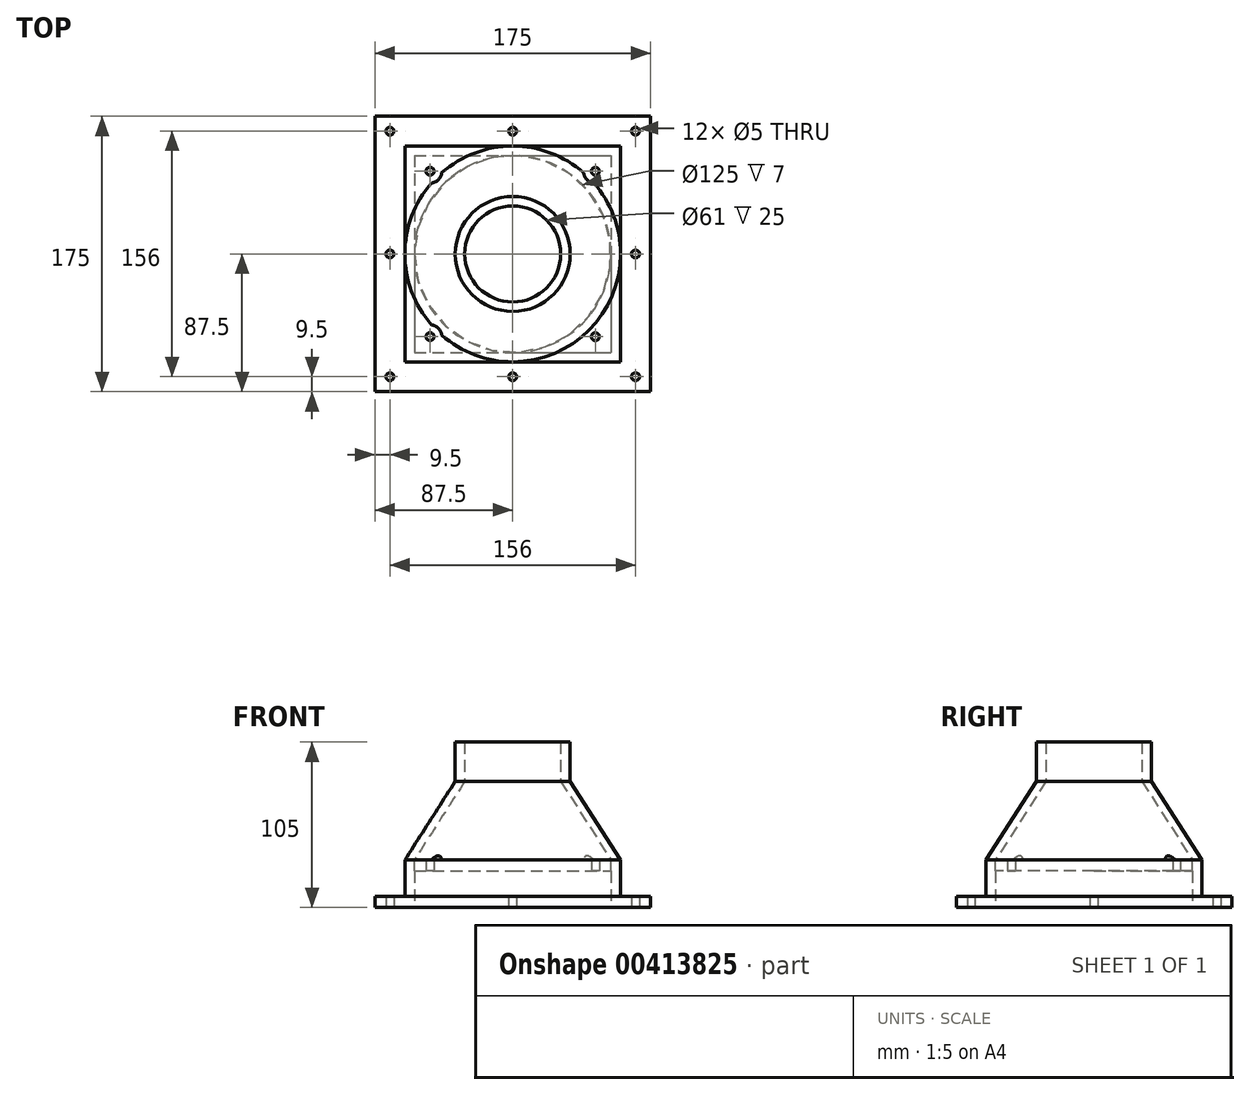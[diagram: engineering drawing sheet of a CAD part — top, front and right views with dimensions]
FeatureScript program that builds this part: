
annotation { "Feature Type Name" : "Feature", "Feature Type Description" : "" }
export const myFeature = defineFeature(function(context is Context, id is Id, definition is map)
    precondition{}
    {
        {
            var Q0;
            Q0=qCreatedBy(makeId("Top.planeOp"),FACE);
            var sketch = newSketch(context, id + "F0", { "sketchPlane" : qUnion([Q0])});
            skLineSegment(sketch, "E0.bottom", {"start": v(-62.5, 62.5) * mm, "end": v(62.5, 62.5) * mm});
            skLineSegment(sketch, "E0.top", {"start": v(-62.5, -62.5) * mm, "end": v(62.5, -62.5) * mm});
            skLineSegment(sketch, "E0.left", {"start": v(-62.5, 62.5) * mm, "end": v(-62.5, -62.5) * mm});
            skLineSegment(sketch, "E0.right", {"start": v(62.5, 62.5) * mm, "end": v(62.5, -62.5) * mm});
            skPoint(sketch, "E0.middle", {"position": v(0, 0) * mm});
            skLineSegment(sketch, "E1.bottom", {"start": v(-52.5, 52.5) * mm, "end": v(52.5, 52.5) * mm, "construction": true});
            skLineSegment(sketch, "E1.top", {"start": v(-52.5, -52.5) * mm, "end": v(52.5, -52.5) * mm, "construction": true});
            skLineSegment(sketch, "E1.left", {"start": v(-52.5, 52.5) * mm, "end": v(-52.5, -52.5) * mm, "construction": true});
            skLineSegment(sketch, "E1.right", {"start": v(52.5, 52.5) * mm, "end": v(52.5, -52.5) * mm, "construction": true});
            skLineSegment(sketch, "E2.bottom", {"start": v(-87.5, 87.5) * mm, "end": v(87.5, 87.5) * mm});
            skLineSegment(sketch, "E2.top", {"start": v(-87.5, -87.5) * mm, "end": v(87.5, -87.5) * mm});
            skLineSegment(sketch, "E2.left", {"start": v(-87.5, 87.5) * mm, "end": v(-87.5, -87.5) * mm});
            skLineSegment(sketch, "E2.right", {"start": v(87.5, 87.5) * mm, "end": v(87.5, -87.5) * mm});
            skLineSegment(sketch, "E3.0", {"start": v(-68.5, 68.5) * mm, "end": v(68.5, 68.5) * mm});
            skLineSegment(sketch, "E3.1", {"start": v(-68.5, 68.5) * mm, "end": v(-68.5, -68.5) * mm});
            skLineSegment(sketch, "E3.2", {"start": v(-68.5, -68.5) * mm, "end": v(68.5, -68.5) * mm});
            skLineSegment(sketch, "E3.3", {"start": v(68.5, 68.5) * mm, "end": v(68.5, -68.5) * mm});
            skCircle(sketch, "E4", {"center": v(0, 0) * mm, "radius": 62.5 * mm});
            skLineSegment(sketch, "E5.0", {"start": v(-78, 78) * mm, "end": v(78, 78) * mm, "construction": true});
            skLineSegment(sketch, "E5.1", {"start": v(-78, 78) * mm, "end": v(-78, -78) * mm, "construction": true});
            skLineSegment(sketch, "E5.2", {"start": v(-78, -78) * mm, "end": v(78, -78) * mm, "construction": true});
            skLineSegment(sketch, "E5.3", {"start": v(78, 78) * mm, "end": v(78, -78) * mm, "construction": true});
            skPoint(sketch, "E6", {"position": v(-78, 0) * mm});
            skPoint(sketch, "E7", {"position": v(0, -78) * mm});
            skPoint(sketch, "E8", {"position": v(78, 0) * mm});
            skPoint(sketch, "E9", {"position": v(0, 78) * mm});
            skSolve(sketch);
        }
        {
            var Q0;
            Q0=makeQuery(id+"F0.imprint","IMPRINT",FACE,{"disambiguationData":[TD([[makeQuery(id+"F0.imprint","IMPRINT",EDGE,{"derivedFrom":sQuery(id+"F0.wireOp",EDGE,"E2.bottom")}),-1.0]])]});
            extrude(context, id + "F1", {"entities" : qUnion([Q0]), "depth" : 7 * mm});
        }
        {
            var Q0;
            Q0=makeQuery(id+"F0.imprint","IMPRINT",FACE,{"disambiguationData":[TD([[makeQuery(id+"F0.imprint","IMPRINT",EDGE,{"derivedFrom":sQuery(id+"F0.wireOp",EDGE,"E0.bottom")}),1.0]])]});
            extrude(context, id + "F2", {"entities" : qUnion([Q0]), "operationType" : NewBodyOperationType.ADD, "depth" : 30 * mm});
        }
        {
            var Q0;
            Q0=makeQuery(id+"F2.opExtrude","CAP_FACE",FACE,{"disambiguationData":[OSD([sQuery(id+"F0.wireOp",EDGE,"E0.bottom"),sQuery(id+"F0.wireOp",EDGE,"E0.top"),sQuery(id+"F0.wireOp",EDGE,"E0.left"),sQuery(id+"F0.wireOp",EDGE,"E0.right"),sQuery(id+"F0.wireOp",EDGE,"E3.0"),sQuery(id+"F0.wireOp",EDGE,"E3.1"),sQuery(id+"F0.wireOp",EDGE,"E3.2"),sQuery(id+"F0.wireOp",EDGE,"E3.3")])],"isStart":false});
            var sketch = newSketch(context, id + "F3", { "sketchPlane" : qUnion([Q0])});
            skCircle(sketch, "E10.0", {"center": v(0, 0) * mm, "radius": 62.5 * mm});
            skLineSegment(sketch, "E11.0", {"start": v(-62.5, 62.5) * mm, "end": v(62.5, 62.5) * mm});
            skLineSegment(sketch, "E11.1", {"start": v(-62.5, 62.5) * mm, "end": v(-62.5, -62.5) * mm});
            skLineSegment(sketch, "E11.2", {"start": v(-62.5, -62.5) * mm, "end": v(62.5, -62.5) * mm});
            skLineSegment(sketch, "E11.3", {"start": v(62.5, 62.5) * mm, "end": v(62.5, -62.5) * mm});
            skCircle(sketch, "E12.0", {"center": v(0, 0) * mm, "radius": 68.5 * mm});
            skSolve(sketch);
        }
        {
            var Q0;
            {var subQ0=sQuery(id+"F3.wireOp",EDGE,"E11.1");var subQ1=sQuery(id+"F3.wireOp",EDGE,"E11.0");var subQ2=makeQuery(id+"F3.imprint","INTERSECT",VERTEX,{"derivedFrom":[subQ1,subQ0]});Q0=makeQuery(id+"F3.imprint","IMPRINT",FACE,{"disambiguationData":[TD([[makeQuery(id+"F3.imprint","IMPRINT",EDGE,{"disambiguationData":[TD([[subQ2,-1.0]])],"derivedFrom":subQ1}),-1.0]])]});}
            var Q1;
            Q1=makeQuery(id+"F3.imprint","IMPRINT",FACE,{"disambiguationData":[TD([[makeQuery(id+"F3.imprint","IMPRINT",EDGE,{"derivedFrom":sQuery(id+"F3.wireOp",EDGE,"E10.0")}),-1.0]])]});
            var Q2;
            {var subQ0=sQuery(id+"F3.wireOp",EDGE,"E11.3");var subQ1=sQuery(id+"F3.wireOp",EDGE,"E11.0");var subQ2=makeQuery(id+"F3.imprint","INTERSECT",VERTEX,{"derivedFrom":[subQ1,subQ0]});Q2=makeQuery(id+"F3.imprint","IMPRINT",FACE,{"disambiguationData":[TD([[makeQuery(id+"F3.imprint","IMPRINT",EDGE,{"disambiguationData":[TD([[subQ2,1.0]])],"derivedFrom":subQ1}),-1.0]])]});}
            var Q3;
            {var subQ0=sQuery(id+"F3.wireOp",EDGE,"E11.3");var subQ1=sQuery(id+"F3.wireOp",EDGE,"E11.2");var subQ2=makeQuery(id+"F3.imprint","INTERSECT",VERTEX,{"derivedFrom":[subQ1,subQ0]});Q3=makeQuery(id+"F3.imprint","IMPRINT",FACE,{"disambiguationData":[TD([[makeQuery(id+"F3.imprint","IMPRINT",EDGE,{"disambiguationData":[TD([[subQ2,1.0]])],"derivedFrom":subQ1}),1.0]])]});}
            var Q4;
            {var subQ0=sQuery(id+"F3.wireOp",EDGE,"E11.2");var subQ1=sQuery(id+"F3.wireOp",EDGE,"E11.1");var subQ2=makeQuery(id+"F3.imprint","INTERSECT",VERTEX,{"derivedFrom":[subQ1,subQ0]});Q4=makeQuery(id+"F3.imprint","IMPRINT",FACE,{"disambiguationData":[TD([[makeQuery(id+"F3.imprint","IMPRINT",EDGE,{"disambiguationData":[TD([[subQ2,1.0]])],"derivedFrom":subQ1}),1.0]])]});}
            extrude(context, id + "F4", {"entities" : qUnion([Q0, Q1, Q2, Q3, Q4]), "operationType" : NewBodyOperationType.ADD, "oppositeDirection" : true, "depth" : 7 * mm});
        }
        {
            var Q0;
            Q0=qCreatedBy(makeId("Front.planeOp"),FACE);
            var sketch = newSketch(context, id + "F5", { "sketchPlane" : qUnion([Q0])});
            skLineSegment(sketch, "E13", {"start": v(0, 0) * mm, "end": v(0, 80) * mm, "construction": true});
            skLineSegment(sketch, "E14", {"start": v(0, 80) * mm, "end": v(36.5, 80) * mm, "construction": true});
            skLineSegment(sketch, "E15", {"start": v(0, 80) * mm, "end": v(-30.5, 80) * mm, "construction": true});
            skLineSegment(sketch, "E16", {"start": v(-30.5, 80) * mm, "end": v(-36.5, 80) * mm, "construction": true});
            skLineSegment(sketch, "E17.0", {"start": v(-68.5, 30) * mm, "end": v(68.5, 30) * mm, "construction": true});
            skLineSegment(sketch, "E18", {"start": v(-68.5, 30) * mm, "end": v(-36.5, 80) * mm});
            skPoint(sketch, "E19", {"position": v(-62.5, 30) * mm});
            skLineSegment(sketch, "E20", {"start": v(-68.5, 30) * mm, "end": v(-62.5, 30) * mm});
            skLineSegment(sketch, "E21", {"start": v(-36.5, 80) * mm, "end": v(-30.5, 80) * mm});
            skLineSegment(sketch, "E22", {"start": v(-30.5, 80) * mm, "end": v(-62.5, 30) * mm});
            skSolve(sketch);
        }
        {
            var Q0;
            Q0=makeQuery(id+"F5.imprint","IMPRINT",FACE,{"disambiguationData":[TD([[makeQuery(id+"F5.imprint","IMPRINT",EDGE,{"derivedFrom":sQuery(id+"F5.wireOp",EDGE,"E18")}),-1.0]])]});
            var Q1;
            Q1=sQuery(id+"F5.wireOp",EDGE,"E13");
            revolve(context, id + "F6", {"operationType" : NewBodyOperationType.ADD, "entities" : qUnion([Q0]), "axis" : qUnion([Q1]), "revolveType" : RevolveType.FULL});
        }
        {
            var Q0;
            Q0=makeQuery(id+"F6.opRevolve","SWEPT_FACE",FACE,{"disambiguationData":[OSD([sQuery(id+"F5.wireOp",EDGE,"E21")])]});
            extrude(context, id + "F7", {"entities" : qUnion([Q0]), "operationType" : NewBodyOperationType.ADD, "depth" : 25 * mm});
        }
        {
            var Q0;
            Q0=sQuery(id+"F0.wireOp",VERTEX,"E1.left.start");
            var Q1;
            Q1=makeQuery(id+"F1.opExtrude","SWEPT_BODY",BODY,{"disambiguationData":[OSD([sQuery(id+"F0.wireOp",EDGE,"E2.bottom"),sQuery(id+"F0.wireOp",EDGE,"E2.top"),sQuery(id+"F0.wireOp",EDGE,"E2.left"),sQuery(id+"F0.wireOp",EDGE,"E2.right"),sQuery(id+"F0.wireOp",EDGE,"E3.0"),sQuery(id+"F0.wireOp",EDGE,"E3.1"),sQuery(id+"F0.wireOp",EDGE,"E3.2"),sQuery(id+"F0.wireOp",EDGE,"E3.3")])]});
            hole(context, id + "F8", {"style" : HoleStyle.SIMPLE, "endStyle" : HoleEndStyle.THROUGH, "oppositeDirection" : true, "holeDiameter" : 5 * mm, "isTappedThrough" : true, "tappedDepth" : 12 * mm, "tapClearance" : 3, "locations" : qUnion([Q0]), "scope" : qUnion([Q1])});
        }
        {
            var Q0;
            Q0=sQuery(id+"F0.wireOp",VERTEX,"E1.bottom.end");
            var Q1;
            Q1=makeQuery(id+"F1.opExtrude","SWEPT_BODY",BODY,{"disambiguationData":[OSD([sQuery(id+"F0.wireOp",EDGE,"E2.bottom"),sQuery(id+"F0.wireOp",EDGE,"E2.top"),sQuery(id+"F0.wireOp",EDGE,"E2.left"),sQuery(id+"F0.wireOp",EDGE,"E2.right"),sQuery(id+"F0.wireOp",EDGE,"E3.0"),sQuery(id+"F0.wireOp",EDGE,"E3.1"),sQuery(id+"F0.wireOp",EDGE,"E3.2"),sQuery(id+"F0.wireOp",EDGE,"E3.3")])]});
            hole(context, id + "F9", {"style" : HoleStyle.SIMPLE, "endStyle" : HoleEndStyle.THROUGH, "oppositeDirection" : true, "holeDiameter" : 5 * mm, "isTappedThrough" : true, "tappedDepth" : 12 * mm, "tapClearance" : 3, "locations" : qUnion([Q0]), "scope" : qUnion([Q1])});
        }
        {
            var Q0;
            Q0=sQuery(id+"F0.wireOp",VERTEX,"E1.top.start");
            var Q1;
            Q1=makeQuery(id+"F1.opExtrude","SWEPT_BODY",BODY,{"disambiguationData":[OSD([sQuery(id+"F0.wireOp",EDGE,"E2.bottom"),sQuery(id+"F0.wireOp",EDGE,"E2.top"),sQuery(id+"F0.wireOp",EDGE,"E2.left"),sQuery(id+"F0.wireOp",EDGE,"E2.right"),sQuery(id+"F0.wireOp",EDGE,"E3.0"),sQuery(id+"F0.wireOp",EDGE,"E3.1"),sQuery(id+"F0.wireOp",EDGE,"E3.2"),sQuery(id+"F0.wireOp",EDGE,"E3.3")])]});
            hole(context, id + "F10", {"style" : HoleStyle.SIMPLE, "endStyle" : HoleEndStyle.THROUGH, "oppositeDirection" : true, "holeDiameter" : 5 * mm, "isTappedThrough" : true, "tappedDepth" : 12 * mm, "tapClearance" : 3, "locations" : qUnion([Q0]), "scope" : qUnion([Q1])});
        }
        {
            var Q0;
            Q0=sQuery(id+"F0.wireOp",VERTEX,"E1.top.end");
            var Q1;
            Q1=makeQuery(id+"F1.opExtrude","SWEPT_BODY",BODY,{"disambiguationData":[OSD([sQuery(id+"F0.wireOp",EDGE,"E2.bottom"),sQuery(id+"F0.wireOp",EDGE,"E2.top"),sQuery(id+"F0.wireOp",EDGE,"E2.left"),sQuery(id+"F0.wireOp",EDGE,"E2.right"),sQuery(id+"F0.wireOp",EDGE,"E3.0"),sQuery(id+"F0.wireOp",EDGE,"E3.1"),sQuery(id+"F0.wireOp",EDGE,"E3.2"),sQuery(id+"F0.wireOp",EDGE,"E3.3")])]});
            hole(context, id + "F11", {"style" : HoleStyle.SIMPLE, "endStyle" : HoleEndStyle.THROUGH, "oppositeDirection" : true, "holeDiameter" : 5 * mm, "isTappedThrough" : true, "tappedDepth" : 12 * mm, "tapClearance" : 3, "locations" : qUnion([Q0]), "scope" : qUnion([Q1])});
        }
        {
            var Q0;
            Q0=sQuery(id+"F0.wireOp",VERTEX,"E5.1.start");
            var Q1;
            Q1=sQuery(id+"F0.wireOp",VERTEX,"E9");
            var Q2;
            Q2=sQuery(id+"F0.wireOp",VERTEX,"E5.3.start");
            var Q3;
            Q3=sQuery(id+"F0.wireOp",VERTEX,"E8");
            var Q4;
            Q4=sQuery(id+"F0.wireOp",VERTEX,"E5.2.end");
            var Q5;
            Q5=sQuery(id+"F0.wireOp",VERTEX,"E7");
            var Q6;
            Q6=sQuery(id+"F0.wireOp",VERTEX,"E5.2.start");
            var Q7;
            Q7=sQuery(id+"F0.wireOp",VERTEX,"E6");
            var Q8;
            Q8=makeQuery(id+"F1.opExtrude","SWEPT_BODY",BODY,{"disambiguationData":[OSD([sQuery(id+"F0.wireOp",EDGE,"E2.bottom"),sQuery(id+"F0.wireOp",EDGE,"E2.top"),sQuery(id+"F0.wireOp",EDGE,"E2.left"),sQuery(id+"F0.wireOp",EDGE,"E2.right"),sQuery(id+"F0.wireOp",EDGE,"E3.0"),sQuery(id+"F0.wireOp",EDGE,"E3.1"),sQuery(id+"F0.wireOp",EDGE,"E3.2"),sQuery(id+"F0.wireOp",EDGE,"E3.3")])]});
            hole(context, id + "F12", {"style" : HoleStyle.SIMPLE, "endStyle" : HoleEndStyle.THROUGH, "oppositeDirection" : true, "holeDiameter" : 5 * mm, "isTappedThrough" : true, "tappedDepth" : 12 * mm, "tapClearance" : 3, "locations" : qUnion([Q0, Q1, Q2, Q3, Q4, Q5, Q6, Q7]), "scope" : qUnion([Q8])});
        }
        {
            var Q0;
            {var subQ0=sQuery(id+"F3.wireOp",EDGE,"E11.3");var subQ1=sQuery(id+"F3.wireOp",EDGE,"E11.0");var subQ2=sQuery(id+"F3.wireOp",EDGE,"E10.0");var subQ3=makeQuery(id+"F4.opExtrude","CAP_FACE",FACE,{"disambiguationData":[OSD([subQ2,subQ1,subQ0])],"isStart":true});var subQ4=sQuery(id+"F0.wireOp",EDGE,"E3.3");var subQ5=sQuery(id+"F3.wireOp",EDGE,"E11.1");var subQ6=makeQuery(id+"F4.opExtrude","CAP_FACE",FACE,{"disambiguationData":[OSD([subQ2,subQ1,subQ5])],"isStart":true});var subQ7=sQuery(id+"F0.wireOp",EDGE,"E3.2");var subQ8=makeQuery(id+"F2.opExtrude","CAP_FACE",FACE,{"disambiguationData":[OSD([sQuery(id+"F0.wireOp",EDGE,"E0.bottom"),sQuery(id+"F0.wireOp",EDGE,"E0.top"),sQuery(id+"F0.wireOp",EDGE,"E0.left"),sQuery(id+"F0.wireOp",EDGE,"E0.right"),sQuery(id+"F0.wireOp",EDGE,"E3.0"),sQuery(id+"F0.wireOp",EDGE,"E3.1"),subQ7,subQ4])],"isStart":false});var subQ9=sQuery(id+"F3.wireOp",EDGE,"E11.2");var subQ10=makeQuery(id+"F4.opExtrude","CAP_FACE",FACE,{"disambiguationData":[OSD([subQ2,subQ5,subQ9])],"isStart":true});var subQ11=makeQuery(id+"F4.opExtrude","CAP_FACE",FACE,{"disambiguationData":[OSD([subQ2,subQ9,subQ0])],"isStart":true});Q0=makeQuery(id+"F6.boolean.opBoolean","SPLIT",FACE,{"disambiguationData":[TD([subQ8,makeQuery(id+"F2.opExtrude","SWEPT_FACE",FACE,{"disambiguationData":[OSD([subQ7])]}),makeQuery(id+"F2.opExtrude","SWEPT_FACE",FACE,{"disambiguationData":[OSD([subQ4])]}),subQ3,subQ6,subQ10,subQ11,makeQuery(id+"F6.opRevolve","SWEPT_FACE",FACE,{"disambiguationData":[OSD([sQuery(id+"F5.wireOp",EDGE,"E18")])]})])],"derivedFrom":makeQuery(id+"F4.boolean.opBoolean","MERGE",FACE,{"derivedFrom":[subQ8,subQ3,subQ6,subQ10,subQ11]})});}
            var sketch = newSketch(context, id + "F13", { "sketchPlane" : qUnion([Q0])});
            skCircle(sketch, "E23.0", {"center": v(52.5, -52.5) * mm, "radius": 2.5 * mm});
            skCircle(sketch, "E24.0", {"center": v(52.5, -52.5) * mm, "radius": 7.5 * mm});
            skCircle(sketch, "E25.0", {"center": v(-52.5, -52.5) * mm, "radius": 7.5 * mm});
            skCircle(sketch, "E26.0", {"center": v(-52.5, 52.5) * mm, "radius": 7.5 * mm});
            skCircle(sketch, "E27.0", {"center": v(52.5, 52.5) * mm, "radius": 7.5 * mm});
            skSolve(sketch);
        }
        {
            var Q0;
            {var subQ0=sQuery(id+"F13.wireOp",EDGE,"E24.0");var subQ1=sQuery(id+"F3.wireOp",EDGE,"E11.3");var subQ2=sQuery(id+"F3.wireOp",EDGE,"E11.0");var subQ3=sQuery(id+"F3.wireOp",EDGE,"E10.0");var subQ4=sQuery(id+"F0.wireOp",EDGE,"E3.3");var subQ5=sQuery(id+"F3.wireOp",EDGE,"E11.1");var subQ6=sQuery(id+"F0.wireOp",EDGE,"E3.2");var subQ7=sQuery(id+"F3.wireOp",EDGE,"E11.2");var subQ8=sQuery(id+"F5.wireOp",EDGE,"E18");var subQ9=makeQuery(id+"F6.boolean.opBoolean","SPLIT",EDGE,{"disambiguationData":[TD([makeQuery(id+"F2.opExtrude","CAP_FACE",FACE,{"disambiguationData":[OSD([sQuery(id+"F0.wireOp",EDGE,"E0.bottom"),sQuery(id+"F0.wireOp",EDGE,"E0.top"),sQuery(id+"F0.wireOp",EDGE,"E0.left"),sQuery(id+"F0.wireOp",EDGE,"E0.right"),sQuery(id+"F0.wireOp",EDGE,"E3.0"),sQuery(id+"F0.wireOp",EDGE,"E3.1"),subQ6,subQ4])],"isStart":false}),makeQuery(id+"F2.opExtrude","SWEPT_FACE",FACE,{"disambiguationData":[OSD([subQ6])]}),makeQuery(id+"F2.opExtrude","SWEPT_FACE",FACE,{"disambiguationData":[OSD([subQ4])]}),makeQuery(id+"F4.opExtrude","CAP_FACE",FACE,{"disambiguationData":[OSD([subQ3,subQ2,subQ1])],"isStart":true}),makeQuery(id+"F4.opExtrude","CAP_FACE",FACE,{"disambiguationData":[OSD([subQ3,subQ2,subQ5])],"isStart":true}),makeQuery(id+"F4.opExtrude","CAP_FACE",FACE,{"disambiguationData":[OSD([subQ3,subQ5,subQ7])],"isStart":true}),makeQuery(id+"F4.opExtrude","CAP_FACE",FACE,{"disambiguationData":[OSD([subQ3,subQ7,subQ1])],"isStart":true}),makeQuery(id+"F6.opRevolve","SWEPT_FACE",FACE,{"disambiguationData":[OSD([subQ8])]})])],"derivedFrom":makeQuery(id+"F6.opRevolve","SWEPT_EDGE",EDGE,{"disambiguationData":[OSD([subQ8,sQuery(id+"F5.wireOp",EDGE,"E20")])]})});var subQ10=makeQuery(id+"F13.imprint","INTERSECT",VERTEX,{"disambiguationData":[OD(0.0)],"derivedFrom":[subQ9,subQ0]});Q0=makeQuery(id+"F13.imprint","IMPRINT",FACE,{"disambiguationData":[TD([[makeQuery(id+"F13.imprint","IMPRINT",EDGE,{"disambiguationData":[TD([[subQ10,1.0]])],"derivedFrom":subQ0}),1.0]])]});}
            var Q1;
            Q1=makeQuery(id+"F13.imprint","IMPRINT",FACE,{"disambiguationData":[TD([[makeQuery(id+"F13.imprint","IMPRINT",EDGE,{"derivedFrom":sQuery(id+"F13.wireOp",EDGE,"E23.0")}),1.0]])]});
            var Q2;
            Q2=makeQuery(id+"F13.imprint","IMPRINT",FACE,{"disambiguationData":[TD([[makeQuery(id+"F13.imprint","IMPRINT",EDGE,{"derivedFrom":sQuery(id+"F13.wireOp",EDGE,"E25.0")}),1.0]])]});
            var Q3;
            Q3=makeQuery(id+"F13.imprint","IMPRINT",FACE,{"disambiguationData":[TD([[makeQuery(id+"F13.imprint","IMPRINT",EDGE,{"derivedFrom":sQuery(id+"F13.wireOp",EDGE,"E26.0")}),1.0]])]});
            var Q4;
            Q4=makeQuery(id+"F13.imprint","IMPRINT",FACE,{"disambiguationData":[TD([[makeQuery(id+"F13.imprint","IMPRINT",EDGE,{"derivedFrom":sQuery(id+"F13.wireOp",EDGE,"E27.0")}),1.0]])]});
            var Q5;
            Q5=sQuery(id+"F13.wireOp",EDGE,"E24.0");
            extrude(context, id + "F14", {"entities" : qUnion([Q0, Q1, Q2, Q3, Q4]), "operationType" : NewBodyOperationType.REMOVE, "surfaceEntities" : qUnion([Q5]), "depth" : 10 * mm});
        }
    });
